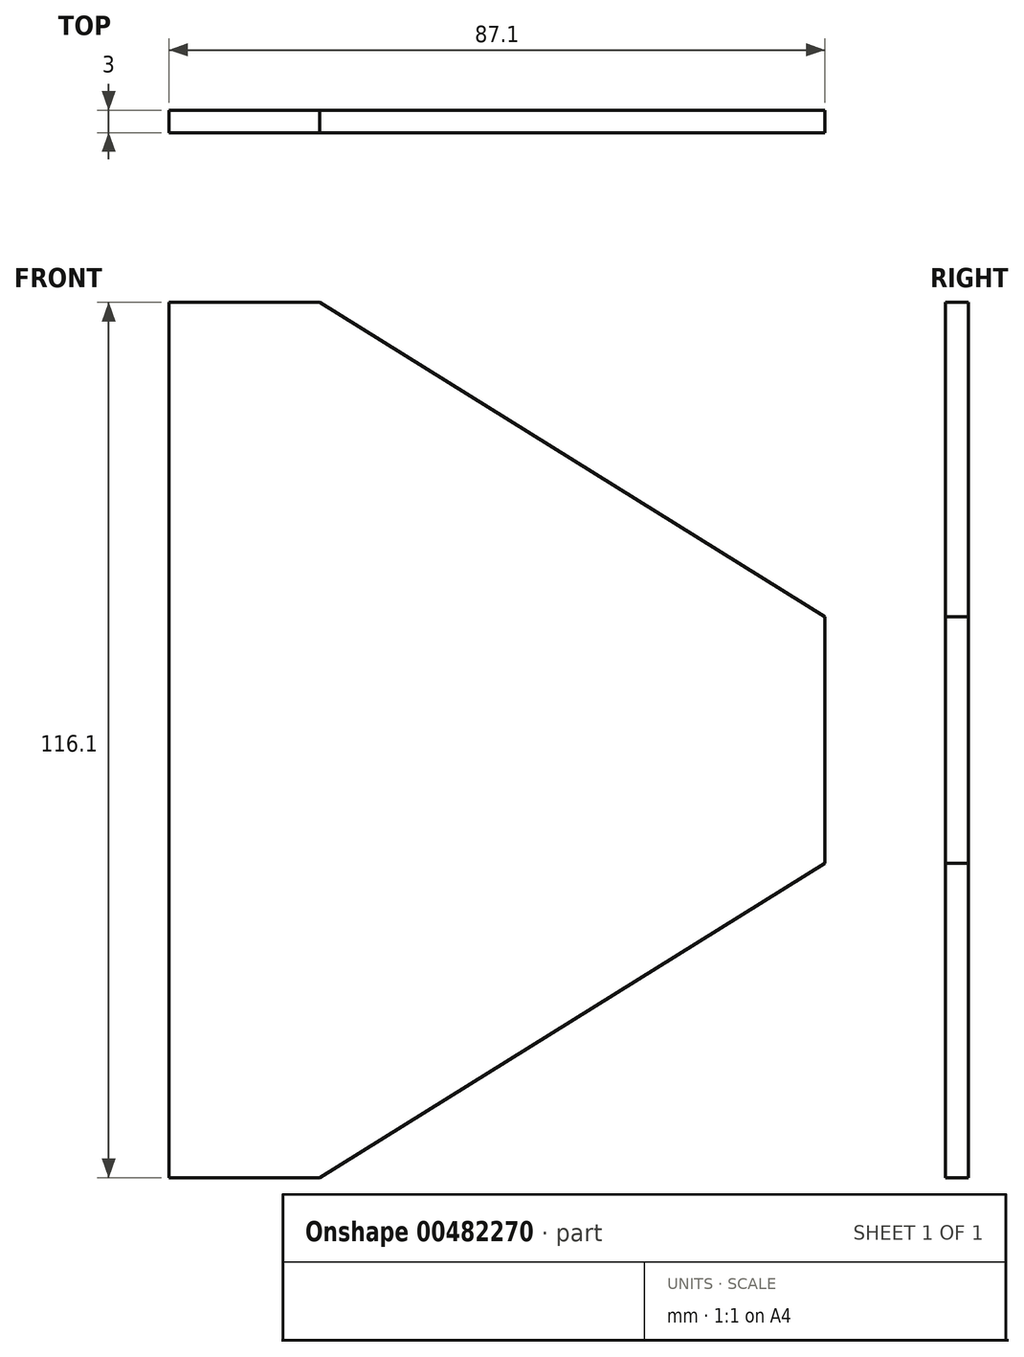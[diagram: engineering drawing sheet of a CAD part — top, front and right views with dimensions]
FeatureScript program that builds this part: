
annotation { "Feature Type Name" : "Feature", "Feature Type Description" : "" }
export const myFeature = defineFeature(function(context is Context, id is Id, definition is map)
    precondition{}
    {
        {
            var Q0;
            Q0=qCreatedBy(makeId("Front.planeOp"),FACE);
            var sketch = newSketch(context, id + "F0", { "sketchPlane" : qUnion([Q0])});
            skLineSegment(sketch, "E0", {"start": v(-67.1, 58.05) * mm, "end": v(-67.1, 0) * mm, "construction": true});
            skLineSegment(sketch, "E1", {"start": v(-67.1, 0) * mm, "end": v(-67.1, -58.05) * mm, "construction": true});
            skLineSegment(sketch, "E2", {"start": v(-67.1, -58.05) * mm, "end": v(0, -16.33) * mm});
            skLineSegment(sketch, "E3", {"start": v(0, -16.33) * mm, "end": v(0, 0) * mm});
            skLineSegment(sketch, "E4", {"start": v(0, 0) * mm, "end": v(0, 16.33) * mm});
            skLineSegment(sketch, "E5", {"start": v(0, 16.33) * mm, "end": v(-67.1, 58.05) * mm});
            skLineSegment(sketch, "E6", {"start": v(-67.1, 58.05) * mm, "end": v(-87.1, 58.05) * mm});
            skLineSegment(sketch, "E7", {"start": v(-87.1, 58.05) * mm, "end": v(-87.1, -58.05) * mm});
            skLineSegment(sketch, "E8", {"start": v(-87.1, -58.05) * mm, "end": v(-67.1, -58.05) * mm});
            skSolve(sketch);
        }
        {
            var Q0;
            Q0=makeQuery(id+"F0.imprint","IMPRINT",FACE,{"disambiguationData":[TD([[makeQuery(id+"F0.imprint","IMPRINT",EDGE,{"derivedFrom":sQuery(id+"F0.wireOp",EDGE,"E2")}),1.0]])]});
            extrude(context, id + "F1", {"entities" : qUnion([Q0]), "depth" : 3 * mm});
        }
    });
